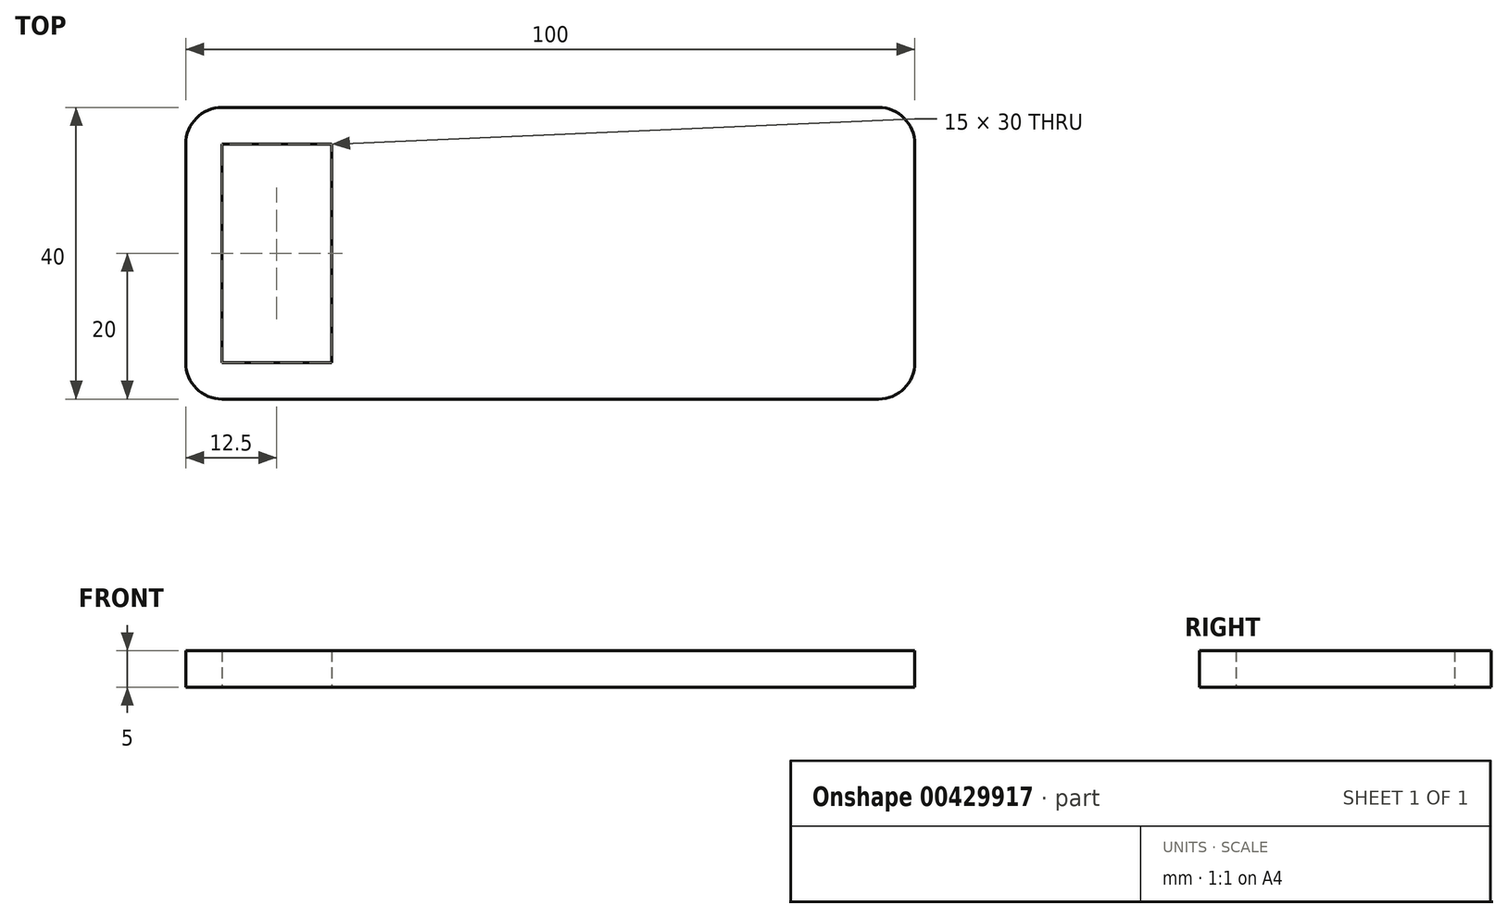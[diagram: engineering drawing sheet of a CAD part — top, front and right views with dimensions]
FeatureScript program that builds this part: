
annotation { "Feature Type Name" : "Feature", "Feature Type Description" : "" }
export const myFeature = defineFeature(function(context is Context, id is Id, definition is map)
    precondition{}
    {
        {
            var Q0;
            Q0=qCreatedBy(makeId("Top.planeOp"),FACE);
            var sketch = newSketch(context, id + "F0", { "sketchPlane" : qUnion([Q0])});
            skLineSegment(sketch, "E0.bottom", {"start": v(50, -20) * mm, "end": v(-50, -20) * mm});
            skLineSegment(sketch, "E0.top", {"start": v(50, 20) * mm, "end": v(-50, 20) * mm});
            skLineSegment(sketch, "E0.left", {"start": v(50, -20) * mm, "end": v(50, 20) * mm});
            skLineSegment(sketch, "E0.right", {"start": v(-50, -20) * mm, "end": v(-50, 20) * mm});
            skPoint(sketch, "E0.middle", {"position": v(0, 0) * mm});
            skLineSegment(sketch, "E1.bottom", {"start": v(-30, 15) * mm, "end": v(-45, 15) * mm});
            skLineSegment(sketch, "E1.top", {"start": v(-30, -15) * mm, "end": v(-45, -15) * mm});
            skLineSegment(sketch, "E1.left", {"start": v(-30, 15) * mm, "end": v(-30, -15) * mm});
            skLineSegment(sketch, "E1.right", {"start": v(-45, 15) * mm, "end": v(-45, -15) * mm});
            skPoint(sketch, "E1.middle", {"position": v(-37.5, 0) * mm});
            skSolve(sketch);
        }
        {
            var Q0;
            Q0 = qSketchRegion(id + "F0", true);
            extrude(context, id + "F1", {"entities" : qUnion([Q0]), "depth" : 5 * mm});
        }
        {
            var Q0;
            Q0=makeQuery(id+"F1.opExtrude","SWEPT_EDGE",EDGE,{"disambiguationData":[OSD([sQuery(id+"F0.wireOp",EDGE,"E0.bottom"),sQuery(id+"F0.wireOp",EDGE,"E0.right")])]});
            var Q1;
            Q1=makeQuery(id+"F1.opExtrude","SWEPT_EDGE",EDGE,{"disambiguationData":[OSD([sQuery(id+"F0.wireOp",EDGE,"E0.bottom"),sQuery(id+"F0.wireOp",EDGE,"E0.left")])]});
            var Q2;
            Q2=makeQuery(id+"F1.opExtrude","SWEPT_EDGE",EDGE,{"disambiguationData":[OSD([sQuery(id+"F0.wireOp",EDGE,"E0.top"),sQuery(id+"F0.wireOp",EDGE,"E0.left")])]});
            var Q3;
            Q3=makeQuery(id+"F1.opExtrude","SWEPT_EDGE",EDGE,{"disambiguationData":[OSD([sQuery(id+"F0.wireOp",EDGE,"E0.top"),sQuery(id+"F0.wireOp",EDGE,"E0.right")])]});
            fillet(context, id + "F2", {"entities" : qUnion([Q0, Q1, Q2, Q3]), "radius" : 5 * mm, "tangentPropagation" : true, "allowEdgeOverflow" : false});
        }
    });
